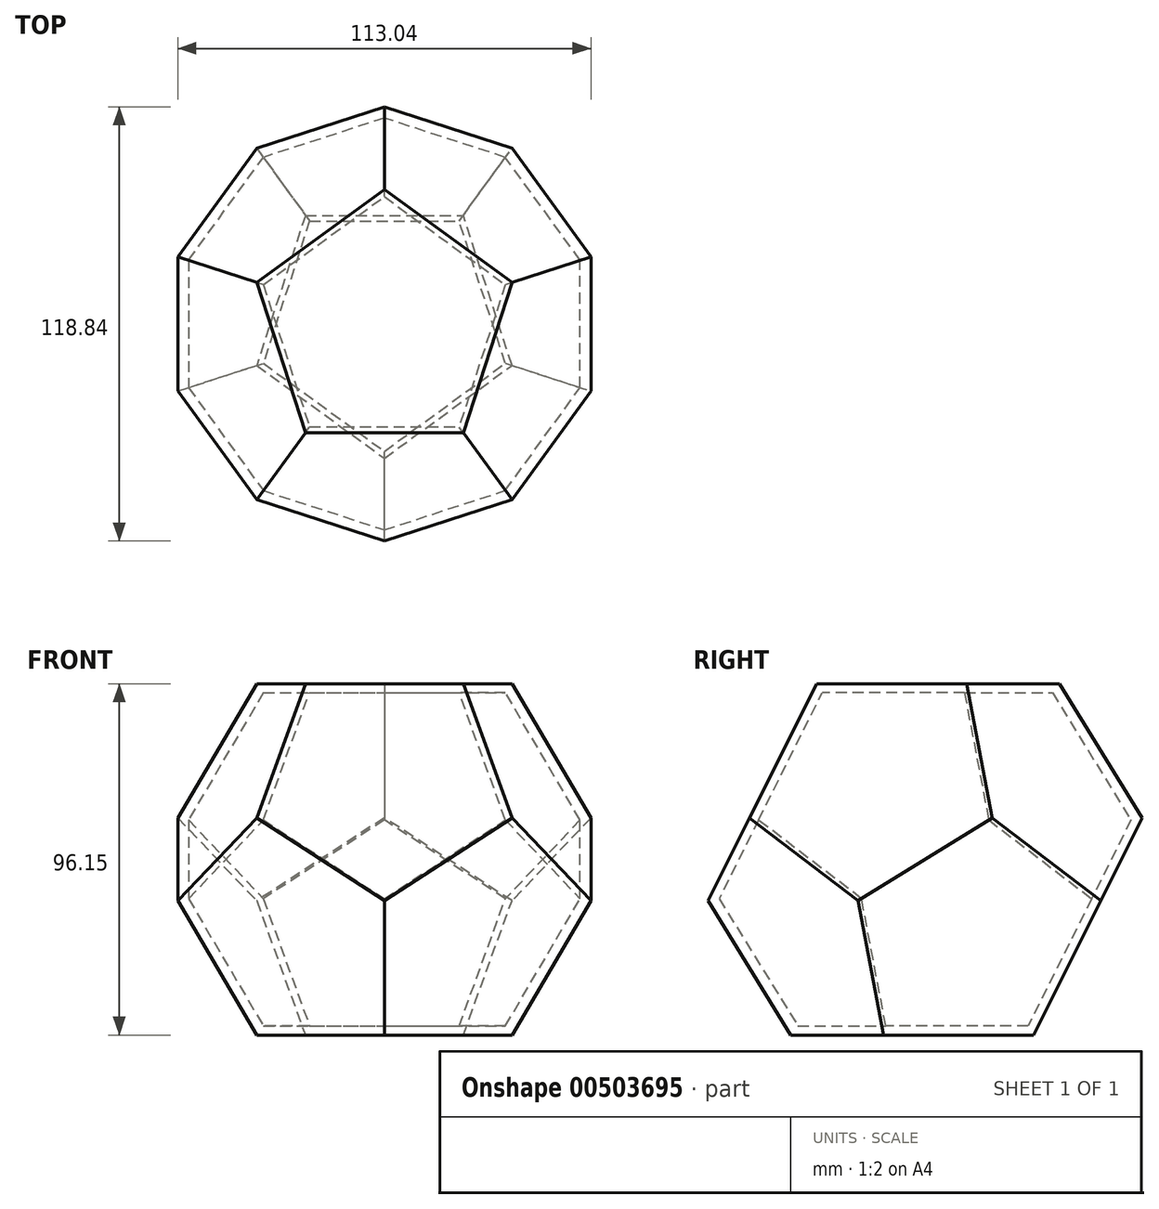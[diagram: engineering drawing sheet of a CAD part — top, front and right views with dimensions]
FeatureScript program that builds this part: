
annotation { "Feature Type Name" : "Feature", "Feature Type Description" : "" }
export const myFeature = defineFeature(function(context is Context, id is Id, definition is map)
    precondition{}
    {
        {
            var Q0;
            Q0=qCreatedBy(makeId("Top.planeOp"),FACE);
            var sketch = newSketch(context, id + "F0", { "sketchPlane" : qUnion([Q0])});
            skCircle(sketch, "E0.cCircle", {"center": v(0, 0) * mm, "radius": 29.71 * mm, "construction": true});
            skLineSegment(sketch, "E0.0", {"start": v(34.93, 11.35) * mm, "end": v(21.59, -29.71) * mm});
            skLineSegment(sketch, "E0.1", {"start": v(21.59, -29.71) * mm, "end": v(-21.59, -29.71) * mm});
            skLineSegment(sketch, "E0.2", {"start": v(-21.59, -29.71) * mm, "end": v(-34.93, 11.35) * mm});
            skLineSegment(sketch, "E0.3", {"start": v(-34.93, 11.35) * mm, "end": v(0, 36.73) * mm});
            skLineSegment(sketch, "E0.4", {"start": v(0, 36.73) * mm, "end": v(34.93, 11.35) * mm});
            skPoint(sketch, "E0.0.midPoint", {"position": v(28.26, -9.18) * mm});
            skLineSegment(sketch, "E1", {"start": v(0, 41.72) * mm, "end": v(0, -38.26) * mm, "construction": true});
            skLineSegment(sketch, "E2", {"start": v(-54.38, 0) * mm, "end": v(61.6, 0) * mm, "construction": true});
            skSolve(sketch);
        }
        {
            var Q0;
            Q0=sQuery(id+"F0.wireOp",EDGE,"E0.2");
            cPlane(context, id + "F1", {"entities" : qUnion([Q0]), "cplaneType" : CPlaneType.LINE_ANGLE, "offset" : 25 * mm, "angle" : 116.57 * degree, "width" : 150 * mm, "height" : 150 * mm});
        }
        {
            var Q0;
            Q0=qCreatedBy(id+"F1.planeOp",FACE);
            var sketch = newSketch(context, id + "F2", { "sketchPlane" : qUnion([Q0])});
            skCircle(sketch, "E3.cCircle", {"center": v(-6.18, -42.55) * mm, "radius": 29.71 * mm, "construction": true});
            skLineSegment(sketch, "E3.0", {"start": v(19.45, -16.25) * mm, "end": v(26.75, -58.8) * mm});
            skLineSegment(sketch, "E3.1", {"start": v(26.75, -58.8) * mm, "end": v(-11.46, -78.9) * mm});
            skLineSegment(sketch, "E3.2", {"start": v(-11.46, -78.9) * mm, "end": v(-42.38, -48.76) * mm});
            skLineSegment(sketch, "E3.3", {"start": v(-42.38, -48.76) * mm, "end": v(-23.27, -10.05) * mm});
            skLineSegment(sketch, "E3.4", {"start": v(-23.27, -10.05) * mm, "end": v(19.45, -16.25) * mm});
            skPoint(sketch, "E3.0.midPoint", {"position": v(23.1, -37.53) * mm});
            skSolve(sketch);
        }
        {
            var Q0;
            Q0=sQuery(id+"F0.wireOp",VERTEX,"E0.1.start");
            var Q1;
            Q1=sQuery(id+"F2.wireOp",VERTEX,"E3.4.start");
            var Q2;
            Q2=sQuery(id+"F2.wireOp",VERTEX,"E3.3.start");
            cPlane(context, id + "F3", {"entities" : qUnion([Q0, Q1, Q2]), "cplaneType" : CPlaneType.THREE_POINT, "offset" : 25 * mm, "oppositeDirection" : true, "width" : 150 * mm, "height" : 150 * mm});
        }
        {
            var Q0;
            Q0=qCreatedBy(id+"F3.planeOp",FACE);
            var sketch = newSketch(context, id + "F4", { "sketchPlane" : qUnion([Q0])});
            skCircle(sketch, "E4.cCircle", {"center": v(0, -43) * mm, "radius": 29.71 * mm, "construction": true});
            skLineSegment(sketch, "E4.0", {"start": v(21.59, -13.29) * mm, "end": v(34.93, -54.35) * mm});
            skLineSegment(sketch, "E4.1", {"start": v(34.93, -54.35) * mm, "end": v(0, -79.73) * mm});
            skLineSegment(sketch, "E4.2", {"start": v(0, -79.73) * mm, "end": v(-34.93, -54.35) * mm});
            skLineSegment(sketch, "E4.3", {"start": v(-34.93, -54.35) * mm, "end": v(-21.59, -13.29) * mm});
            skLineSegment(sketch, "E4.4", {"start": v(-21.59, -13.29) * mm, "end": v(21.59, -13.29) * mm});
            skPoint(sketch, "E4.0.midPoint", {"position": v(28.26, -33.82) * mm});
            skSolve(sketch);
        }
        {
            var Q0;
            Q0=sQuery(id+"F4.wireOp",VERTEX,"E4.2.start");
            var Q1;
            Q1=sQuery(id+"F2.wireOp",VERTEX,"E3.3.start");
            var Q2;
            Q2=sQuery(id+"F2.wireOp",VERTEX,"E3.2.start");
            cPlane(context, id + "F5", {"entities" : qUnion([Q0, Q1, Q2]), "cplaneType" : CPlaneType.THREE_POINT, "offset" : 25 * mm, "width" : 150 * mm, "height" : 150 * mm});
        }
        {
            var Q0;
            Q0=qCreatedBy(id+"F5.planeOp",FACE);
            var sketch = newSketch(context, id + "F6", { "sketchPlane" : qUnion([Q0])});
            skCircle(sketch, "E5.cCircle", {"center": v(-13.29, -40.9) * mm, "radius": 29.71 * mm, "construction": true});
            skLineSegment(sketch, "E5.0", {"start": v(-1.94, -5.97) * mm, "end": v(23.44, -40.9) * mm});
            skLineSegment(sketch, "E5.1", {"start": v(23.44, -40.9) * mm, "end": v(-1.94, -75.82) * mm});
            skLineSegment(sketch, "E5.2", {"start": v(-1.94, -75.82) * mm, "end": v(-43, -62.48) * mm});
            skLineSegment(sketch, "E5.3", {"start": v(-43, -62.48) * mm, "end": v(-43, -19.3) * mm});
            skLineSegment(sketch, "E5.4", {"start": v(-43, -19.3) * mm, "end": v(-1.94, -5.97) * mm});
            skPoint(sketch, "E5.0.midPoint", {"position": v(10.75, -23.43) * mm});
            skSolve(sketch);
        }
        {
            var Q0;
            Q0=sQuery(id+"F4.wireOp",VERTEX,"E4.3.start");
            var Q1;
            Q1=sQuery(id+"F6.wireOp",VERTEX,"E5.3.end");
            var Q2;
            Q2=sQuery(id+"F6.wireOp",VERTEX,"E5.3.start");
            cPlane(context, id + "F7", {"entities" : qUnion([Q0, Q1, Q2]), "cplaneType" : CPlaneType.THREE_POINT, "offset" : 25 * mm, "width" : 150 * mm, "height" : 150 * mm});
        }
        {
            var Q0;
            Q0=qCreatedBy(id+"F7.planeOp",FACE);
            var sketch = newSketch(context, id + "F8", { "sketchPlane" : qUnion([Q0])});
            skCircle(sketch, "E6.cCircle", {"center": v(13.29, -40.9) * mm, "radius": 29.71 * mm, "construction": true});
            skLineSegment(sketch, "E6.0", {"start": v(1.94, -5.97) * mm, "end": v(43, -19.3) * mm});
            skLineSegment(sketch, "E6.1", {"start": v(43, -19.3) * mm, "end": v(43, -62.48) * mm});
            skLineSegment(sketch, "E6.2", {"start": v(43, -62.48) * mm, "end": v(1.94, -75.82) * mm});
            skLineSegment(sketch, "E6.3", {"start": v(1.94, -75.82) * mm, "end": v(-23.44, -40.9) * mm});
            skLineSegment(sketch, "E6.4", {"start": v(-23.44, -40.9) * mm, "end": v(1.94, -5.97) * mm});
            skPoint(sketch, "E6.0.midPoint", {"position": v(22.47, -12.64) * mm});
            skSolve(sketch);
        }
        {
            var Q0;
            Q0=sQuery(id+"F4.wireOp",VERTEX,"E4.4.start");
            var Q1;
            Q1=sQuery(id+"F8.wireOp",VERTEX,"E6.0.start");
            var Q2;
            Q2=sQuery(id+"F8.wireOp",VERTEX,"E6.4.start");
            cPlane(context, id + "F9", {"entities" : qUnion([Q0, Q1, Q2]), "cplaneType" : CPlaneType.THREE_POINT, "offset" : 25 * mm, "width" : 150 * mm, "height" : 150 * mm});
        }
        {
            var Q0;
            Q0=qCreatedBy(id+"F9.planeOp",FACE);
            var sketch = newSketch(context, id + "F10", { "sketchPlane" : qUnion([Q0])});
            skCircle(sketch, "E7.cCircle", {"center": v(6.18, -42.55) * mm, "radius": 29.71 * mm, "construction": true});
            skLineSegment(sketch, "E7.0", {"start": v(-19.45, -16.25) * mm, "end": v(23.27, -10.05) * mm});
            skLineSegment(sketch, "E7.1", {"start": v(23.27, -10.05) * mm, "end": v(42.38, -48.76) * mm});
            skLineSegment(sketch, "E7.2", {"start": v(42.38, -48.76) * mm, "end": v(11.46, -78.9) * mm});
            skLineSegment(sketch, "E7.3", {"start": v(11.46, -78.9) * mm, "end": v(-26.75, -58.8) * mm});
            skLineSegment(sketch, "E7.4", {"start": v(-26.75, -58.8) * mm, "end": v(-19.45, -16.25) * mm});
            skPoint(sketch, "E7.0.midPoint", {"position": v(1.91, -13.15) * mm});
            skSolve(sketch);
        }
        {
            var Q0;
            Q0=sQuery(id+"F0.wireOp",VERTEX,"E0.4.start");
            var Q1;
            Q1=sQuery(id+"F10.wireOp",VERTEX,"E7.0.start");
            var Q2;
            Q2=sQuery(id+"F10.wireOp",VERTEX,"E7.4.start");
            cPlane(context, id + "F11", {"entities" : qUnion([Q0, Q1, Q2]), "cplaneType" : CPlaneType.THREE_POINT, "offset" : 25 * mm, "width" : 150 * mm, "height" : 150 * mm});
        }
        {
            var Q0;
            Q0=qCreatedBy(id+"F11.planeOp",FACE);
            var sketch = newSketch(context, id + "F12", { "sketchPlane" : qUnion([Q0])});
            skCircle(sketch, "E8.cCircle", {"center": v(13.29, -40.9) * mm, "radius": 29.71 * mm, "construction": true});
            skLineSegment(sketch, "E8.0", {"start": v(-16.42, -19.3) * mm, "end": v(24.64, -5.97) * mm});
            skLineSegment(sketch, "E8.1", {"start": v(24.64, -5.97) * mm, "end": v(50.01, -40.9) * mm});
            skLineSegment(sketch, "E8.2", {"start": v(50.01, -40.9) * mm, "end": v(24.64, -75.82) * mm});
            skLineSegment(sketch, "E8.3", {"start": v(24.64, -75.82) * mm, "end": v(-16.42, -62.48) * mm});
            skLineSegment(sketch, "E8.4", {"start": v(-16.42, -62.48) * mm, "end": v(-16.42, -19.3) * mm});
            skPoint(sketch, "E8.0.midPoint", {"position": v(4.1, -12.64) * mm});
            skSolve(sketch);
        }
        {
            var Q0;
            Q0=sQuery(id+"F2.wireOp",VERTEX,"E3.0.start");
            var Q1;
            Q1=sQuery(id+"F12.wireOp",VERTEX,"E8.0.start");
            var Q2;
            Q2=sQuery(id+"F12.wireOp",VERTEX,"E8.4.start");
            cPlane(context, id + "F13", {"entities" : qUnion([Q0, Q1, Q2]), "cplaneType" : CPlaneType.THREE_POINT, "offset" : 25 * mm, "width" : 150 * mm, "height" : 150 * mm});
        }
        {
            var Q0;
            Q0=qCreatedBy(id+"F13.planeOp",FACE);
            var sketch = newSketch(context, id + "F14", { "sketchPlane" : qUnion([Q0])});
            skCircle(sketch, "E9.cCircle", {"center": v(-13.29, -40.9) * mm, "radius": 29.71 * mm, "construction": true});
            skLineSegment(sketch, "E9.0", {"start": v(-50.01, -40.9) * mm, "end": v(-24.64, -5.97) * mm});
            skLineSegment(sketch, "E9.1", {"start": v(-24.64, -5.97) * mm, "end": v(16.42, -19.3) * mm});
            skLineSegment(sketch, "E9.2", {"start": v(16.42, -19.3) * mm, "end": v(16.42, -62.48) * mm});
            skLineSegment(sketch, "E9.3", {"start": v(16.42, -62.48) * mm, "end": v(-24.64, -75.82) * mm});
            skLineSegment(sketch, "E9.4", {"start": v(-24.64, -75.82) * mm, "end": v(-50.01, -40.9) * mm});
            skPoint(sketch, "E9.0.midPoint", {"position": v(-37.33, -23.43) * mm});
            skSolve(sketch);
        }
        {
            var Q0;
            Q0=sQuery(id+"F6.wireOp",VERTEX,"E5.1.start");
            var Q1;
            Q1=sQuery(id+"F14.wireOp",VERTEX,"E9.0.start");
            var Q2;
            Q2=sQuery(id+"F14.wireOp",VERTEX,"E9.4.start");
            cPlane(context, id + "F15", {"entities" : qUnion([Q0, Q1, Q2]), "cplaneType" : CPlaneType.THREE_POINT, "offset" : 25 * mm, "width" : 150 * mm, "height" : 150 * mm});
        }
        {
            var Q0;
            Q0=qCreatedBy(id+"F15.planeOp",FACE);
            var sketch = newSketch(context, id + "F16", { "sketchPlane" : qUnion([Q0])});
            skCircle(sketch, "E10.cCircle", {"center": v(-6.18, -42.55) * mm, "radius": 29.71 * mm, "construction": true});
            skLineSegment(sketch, "E10.0", {"start": v(-39.12, -26.3) * mm, "end": v(-0.9, -6.2) * mm});
            skLineSegment(sketch, "E10.1", {"start": v(-0.9, -6.2) * mm, "end": v(30.01, -36.34) * mm});
            skLineSegment(sketch, "E10.2", {"start": v(30.01, -36.34) * mm, "end": v(10.9, -75.06) * mm});
            skLineSegment(sketch, "E10.3", {"start": v(10.9, -75.06) * mm, "end": v(-31.82, -68.85) * mm});
            skLineSegment(sketch, "E10.4", {"start": v(-31.82, -68.85) * mm, "end": v(-39.12, -26.3) * mm});
            skPoint(sketch, "E10.0.midPoint", {"position": v(-20, -16.25) * mm});
            skSolve(sketch);
        }
        {
            var Q0;
            Q0=sQuery(id+"F12.wireOp",VERTEX,"E8.1.end");
            var Q1;
            Q1=sQuery(id+"F10.wireOp",VERTEX,"E7.3.start");
            var Q2;
            Q2=sQuery(id+"F8.wireOp",VERTEX,"E6.3.start");
            cPlane(context, id + "F17", {"entities" : qUnion([Q0, Q1, Q2]), "cplaneType" : CPlaneType.THREE_POINT, "offset" : 25 * mm, "width" : 150 * mm, "height" : 150 * mm});
        }
        {
            var Q0;
            Q0=qCreatedBy(id+"F17.planeOp",FACE);
            var sketch = newSketch(context, id + "F18", { "sketchPlane" : qUnion([Q0])});
            skCircle(sketch, "E11.cCircle", {"center": v(6.18, -42.55) * mm, "radius": 29.71 * mm, "construction": true});
            skLineSegment(sketch, "E11.0", {"start": v(-30.01, -36.34) * mm, "end": v(0.9, -6.2) * mm});
            skLineSegment(sketch, "E11.1", {"start": v(0.9, -6.2) * mm, "end": v(39.12, -26.3) * mm});
            skLineSegment(sketch, "E11.2", {"start": v(39.12, -26.3) * mm, "end": v(31.82, -68.85) * mm});
            skLineSegment(sketch, "E11.3", {"start": v(31.82, -68.85) * mm, "end": v(-10.9, -75.06) * mm});
            skLineSegment(sketch, "E11.4", {"start": v(-10.9, -75.06) * mm, "end": v(-30.01, -36.34) * mm});
            skPoint(sketch, "E11.0.midPoint", {"position": v(-14.56, -21.28) * mm});
            skSolve(sketch);
        }
        {
            var Q0;
            Q0=sQuery(id+"F18.wireOp",VERTEX,"E11.4.start");
            var Q1;
            Q1=sQuery(id+"F18.wireOp",VERTEX,"E11.3.start");
            var Q2;
            Q2=sQuery(id+"F8.wireOp",VERTEX,"E6.2.start");
            cPlane(context, id + "F19", {"entities" : qUnion([Q0, Q1, Q2]), "cplaneType" : CPlaneType.THREE_POINT, "offset" : 25 * mm, "width" : 150 * mm, "height" : 150 * mm});
        }
        {
            var Q0;
            Q0=qCreatedBy(id+"F19.planeOp",FACE);
            var sketch = newSketch(context, id + "F20", { "sketchPlane" : qUnion([Q0])});
            skCircle(sketch, "E12.cCircle", {"center": v(0, 0) * mm, "radius": 29.71 * mm, "construction": true});
            skLineSegment(sketch, "E12.0", {"start": v(-34.93, -11.35) * mm, "end": v(-21.59, 29.71) * mm});
            skLineSegment(sketch, "E12.1", {"start": v(-21.59, 29.71) * mm, "end": v(21.59, 29.71) * mm});
            skLineSegment(sketch, "E12.2", {"start": v(21.59, 29.71) * mm, "end": v(34.93, -11.35) * mm});
            skLineSegment(sketch, "E12.3", {"start": v(34.93, -11.35) * mm, "end": v(0, -36.73) * mm});
            skLineSegment(sketch, "E12.4", {"start": v(0, -36.73) * mm, "end": v(-34.93, -11.35) * mm});
            skPoint(sketch, "E12.0.midPoint", {"position": v(-28.26, 9.18) * mm});
            skSolve(sketch);
        }
        {
            var Q0;
            Q0=sQuery(id+"F20.wireOp",VERTEX,"E12.2.start");
            var Q1;
            Q1=sQuery(id+"F20.wireOp",VERTEX,"E12.1.start");
            var Q2;
            Q2=sQuery(id+"F14.wireOp",VERTEX,"E9.4.start");
            cPlane(context, id + "F21", {"entities" : qUnion([Q0, Q1, Q2]), "cplaneType" : CPlaneType.THREE_POINT, "offset" : 25 * mm, "width" : 150 * mm, "height" : 150 * mm});
        }
        {
            var Q0;
            Q0=qCreatedBy(id+"F21.planeOp",FACE);
            var sketch = newSketch(context, id + "F22", { "sketchPlane" : qUnion([Q0])});
            skCircle(sketch, "E13.cCircle", {"center": v(0, -43) * mm, "radius": 29.71 * mm, "construction": true});
            skLineSegment(sketch, "E13.0", {"start": v(-34.93, -31.65) * mm, "end": v(0, -6.27) * mm});
            skLineSegment(sketch, "E13.1", {"start": v(0, -6.27) * mm, "end": v(34.93, -31.65) * mm});
            skLineSegment(sketch, "E13.2", {"start": v(34.93, -31.65) * mm, "end": v(21.59, -72.71) * mm});
            skLineSegment(sketch, "E13.3", {"start": v(21.59, -72.71) * mm, "end": v(-21.59, -72.71) * mm});
            skLineSegment(sketch, "E13.4", {"start": v(-21.59, -72.71) * mm, "end": v(-34.93, -31.65) * mm});
            skPoint(sketch, "E13.0.midPoint", {"position": v(-17.46, -18.96) * mm});
            skSolve(sketch);
        }
        {
            var Q0;
            Q0=makeQuery(id+"F2.imprint","IMPRINT",FACE,{"disambiguationData":[TD([[makeQuery(id+"F2.imprint","IMPRINT",EDGE,{"derivedFrom":sQuery(id+"F2.wireOp",EDGE,"E3.0")}),-1.0]])]});
            extrude(context, id + "F23", {"entities" : qUnion([Q0]), "depth" : 2.5 * mm});
        }
        {
            var Q0;
            Q0=makeQuery(id+"F4.imprint","IMPRINT",FACE,{"disambiguationData":[TD([[makeQuery(id+"F4.imprint","IMPRINT",EDGE,{"derivedFrom":sQuery(id+"F4.wireOp",EDGE,"E4.0")}),-1.0]])]});
            extrude(context, id + "F24", {"entities" : qUnion([Q0]), "operationType" : NewBodyOperationType.ADD, "depth" : 2.5 * mm});
        }
        {
            var Q0;
            Q0=makeQuery(id+"F0.imprint","IMPRINT",FACE,{"disambiguationData":[TD([[makeQuery(id+"F0.imprint","IMPRINT",EDGE,{"derivedFrom":sQuery(id+"F0.wireOp",EDGE,"E0.0")}),-1.0]])]});
            extrude(context, id + "F25", {"entities" : qUnion([Q0]), "operationType" : NewBodyOperationType.ADD, "oppositeDirection" : true, "depth" : 2.5 * mm});
        }
        {
            var Q0;
            Q0=makeQuery(id+"F10.imprint","IMPRINT",FACE,{"disambiguationData":[TD([[makeQuery(id+"F10.imprint","IMPRINT",EDGE,{"derivedFrom":sQuery(id+"F10.wireOp",EDGE,"E7.0")}),-1.0]])]});
            extrude(context, id + "F26", {"entities" : qUnion([Q0]), "operationType" : NewBodyOperationType.ADD, "depth" : 2.5 * mm});
        }
        {
            var Q0;
            Q0=makeQuery(id+"F8.imprint","IMPRINT",FACE,{"disambiguationData":[TD([[makeQuery(id+"F8.imprint","IMPRINT",EDGE,{"derivedFrom":sQuery(id+"F8.wireOp",EDGE,"E6.0")}),-1.0]])]});
            extrude(context, id + "F27", {"entities" : qUnion([Q0]), "operationType" : NewBodyOperationType.ADD, "depth" : 2.5 * mm});
        }
        {
            var Q0;
            Q0=makeQuery(id+"F6.imprint","IMPRINT",FACE,{"disambiguationData":[TD([[makeQuery(id+"F6.imprint","IMPRINT",EDGE,{"derivedFrom":sQuery(id+"F6.wireOp",EDGE,"E5.0")}),-1.0]])]});
            extrude(context, id + "F28", {"entities" : qUnion([Q0]), "operationType" : NewBodyOperationType.ADD, "depth" : 2.5 * mm});
        }
        {
            var Q0;
            Q0=makeQuery(id+"F16.imprint","IMPRINT",FACE,{"disambiguationData":[TD([[makeQuery(id+"F16.imprint","IMPRINT",EDGE,{"derivedFrom":sQuery(id+"F16.wireOp",EDGE,"E10.0")}),-1.0]])]});
            extrude(context, id + "F29", {"entities" : qUnion([Q0]), "operationType" : NewBodyOperationType.ADD, "depth" : 2.5 * mm});
        }
        {
            var Q0;
            Q0=makeQuery(id+"F14.imprint","IMPRINT",FACE,{"disambiguationData":[TD([[makeQuery(id+"F14.imprint","IMPRINT",EDGE,{"derivedFrom":sQuery(id+"F14.wireOp",EDGE,"E9.0")}),-1.0]])]});
            extrude(context, id + "F30", {"entities" : qUnion([Q0]), "operationType" : NewBodyOperationType.ADD, "depth" : 2.5 * mm});
        }
        {
            var Q0;
            Q0=makeQuery(id+"F12.imprint","IMPRINT",FACE,{"disambiguationData":[TD([[makeQuery(id+"F12.imprint","IMPRINT",EDGE,{"derivedFrom":sQuery(id+"F12.wireOp",EDGE,"E8.0")}),-1.0]])]});
            extrude(context, id + "F31", {"entities" : qUnion([Q0]), "operationType" : NewBodyOperationType.ADD, "depth" : 2.5 * mm});
        }
        {
            var Q0;
            Q0=makeQuery(id+"F18.imprint","IMPRINT",FACE,{"disambiguationData":[TD([[makeQuery(id+"F18.imprint","IMPRINT",EDGE,{"derivedFrom":sQuery(id+"F18.wireOp",EDGE,"E11.0")}),-1.0]])]});
            extrude(context, id + "F32", {"entities" : qUnion([Q0]), "operationType" : NewBodyOperationType.ADD, "depth" : 2.5 * mm});
        }
        {
            var Q0;
            Q0=makeQuery(id+"F20.imprint","IMPRINT",FACE,{"disambiguationData":[TD([[makeQuery(id+"F20.imprint","IMPRINT",EDGE,{"derivedFrom":sQuery(id+"F20.wireOp",EDGE,"E12.0")}),-1.0]])]});
            extrude(context, id + "F33", {"entities" : qUnion([Q0]), "operationType" : NewBodyOperationType.ADD, "depth" : 2.5 * mm});
        }
        {
            var Q0;
            Q0=makeQuery(id+"F22.imprint","IMPRINT",FACE,{"disambiguationData":[TD([[makeQuery(id+"F22.imprint","IMPRINT",EDGE,{"derivedFrom":sQuery(id+"F22.wireOp",EDGE,"E13.0")}),-1.0]])]});
            extrude(context, id + "F34", {"entities" : qUnion([Q0]), "operationType" : NewBodyOperationType.ADD, "depth" : 2.5 * mm});
        }
    });
